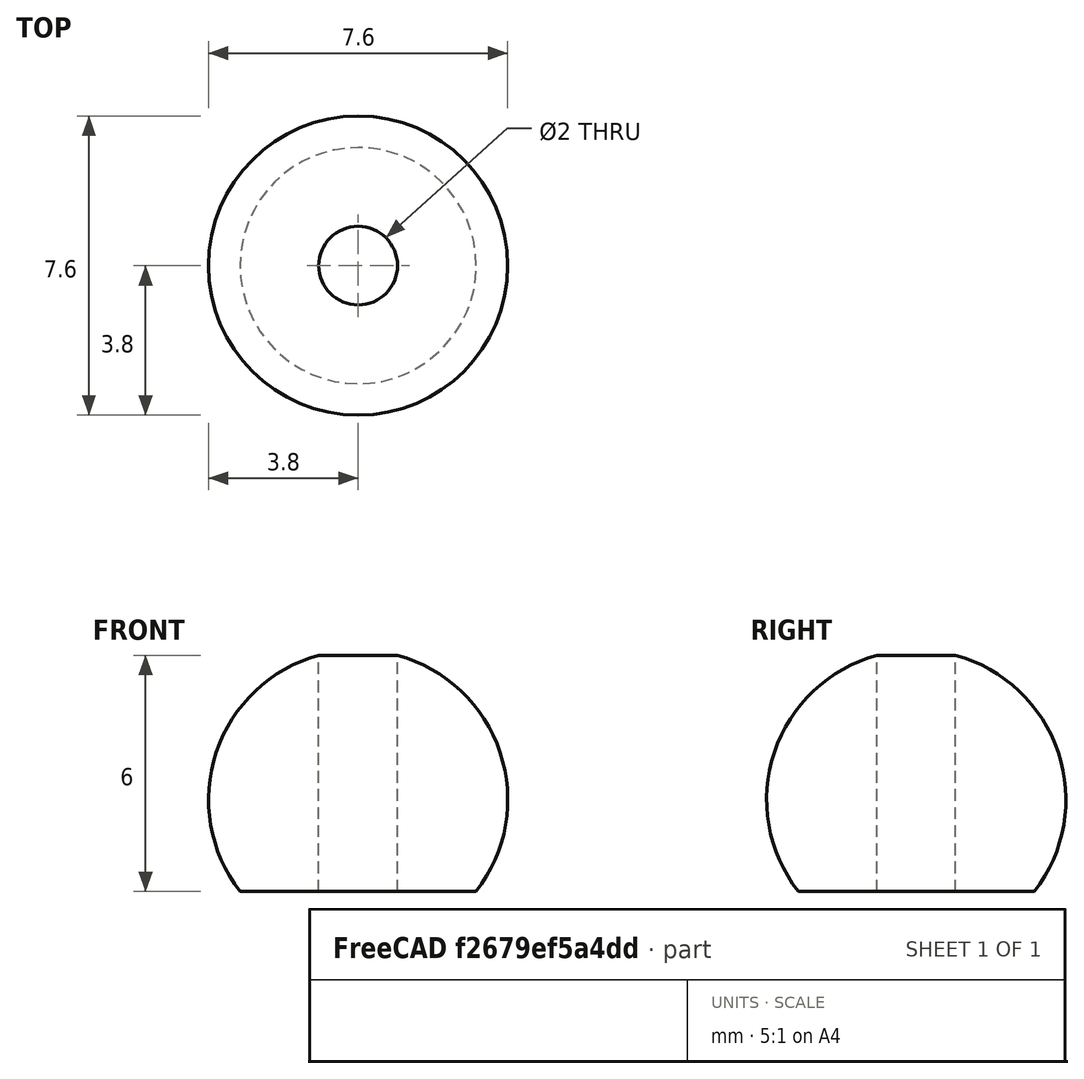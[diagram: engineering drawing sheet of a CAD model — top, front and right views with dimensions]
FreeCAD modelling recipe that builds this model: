
FCSTD DOCUMENT  (FreeCAD 1.1R39153 (Git))
Label: Полусфера
License: All rights reserved
LicenseURL: https://en.wikipedia.org/wiki/All_rights_reserved
objects: Sketcher::SketchObject×1, PartDesign::Revolution×1, PartDesign::Body×1
note: 6 computed .brp shape members not serialized (recipe doc carries the construction recipe); baked Part::Feature solids carry a one-line shape summary decoded from their .brp

FEATURE [Sketcher::SketchObject] Sketch
  ArcFitTolerance = 1e-06
  AttachmentSupport = -> [XZ_Plane]
  FullyConstrained = true
  MakeInternals = false
  MapMode = 5
  Placement = pos=(0,0,0) rot=(1,0,0;1.5708rad)
  sketch-geometry (3):
    g0: ArcOfCircle CenterX=0 CenterY=2.33333 CenterZ=0 NormalX=0 NormalY=0 NormalZ=1 AngleXU=0 Radius=3.80058 StartAngle=1.83705 EndAngle=3.80264
    g1: LineSegment StartX=-3 StartY=0 StartZ=0 EndX=-1 EndY=0 EndZ=0
    g2: LineSegment StartX=-1 StartY=0 StartZ=0 EndX=-1 EndY=6 EndZ=0
  constraints (10):
    c: PointOnObject(g0,g-1)
    c: Coincident(g1,g0)
    c: Horizontal(g1)
    c: Coincident(g2,g1)
    c: Vertical(g2)
    c: Coincident(g0,g2)
    c: DistanceX(g0,g-1) = 3
    c: DistanceY(g2,g2) = 6
    c: DistanceX(g1,g-1) = 1
    c: PointOnObject(g0,g-2)
FEATURE [PartDesign::Revolution] Revolution
  Angle = 360
  Angle2 = 60
  Axis = (0,2e-16,1)
  Base = (0,0,0)
  Placement = pos=(0,0,0) rot=(1,0,0;1.5708rad)
  Profile = -> Sketch
  ReferenceAxis = -> Sketch [V_Axis]
  Refine = true
  Suppressed = false
  Type = 0
FEATURE [PartDesign::Body] Body  label="Тело"
  AllowCompound = false
  Group = -> [Sketch,Revolution]
  Origin = -> Origin
  Tip = -> Revolution
